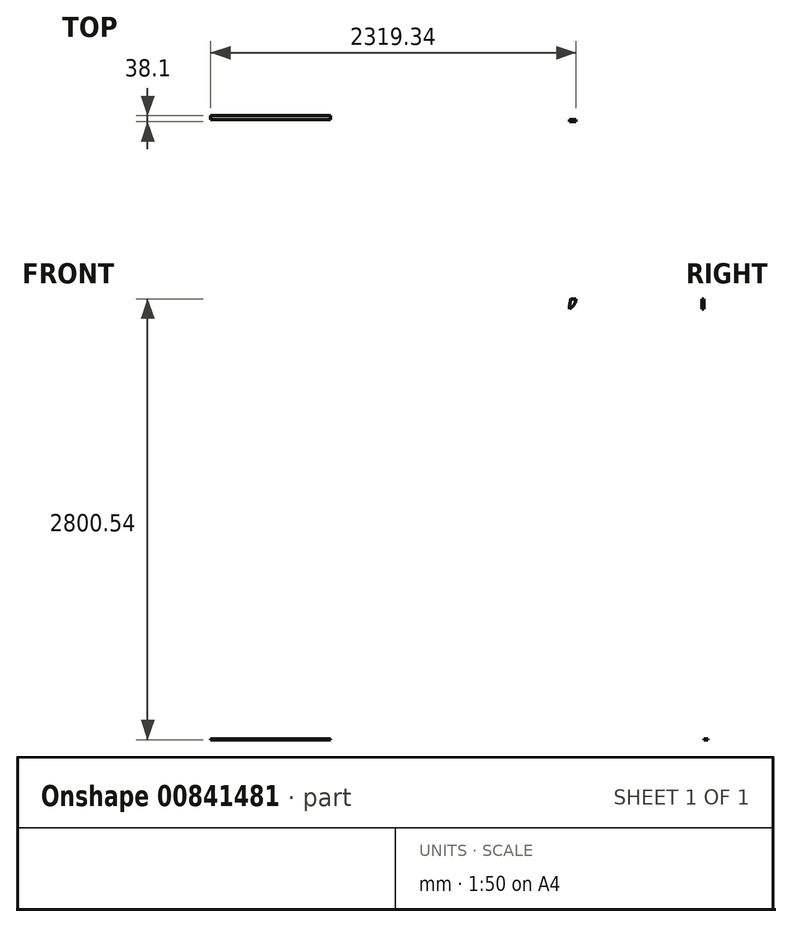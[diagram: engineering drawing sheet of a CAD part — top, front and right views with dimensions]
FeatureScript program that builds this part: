
annotation { "Feature Type Name" : "Feature", "Feature Type Description" : "" }
export const myFeature = defineFeature(function(context is Context, id is Id, definition is map)
    precondition{}
    {
        {
            var Q0;
            Q0=qCreatedBy(makeId("Front.planeOp"),FACE);
            var sketch = newSketch(context, id + "F0", { "sketchPlane" : qUnion([Q0])});
            skLineSegment(sketch, "E0.bottom", {"start": v(-2732.86, 2615) * mm, "end": v(264.34, 2615) * mm});
            skLineSegment(sketch, "E0.top", {"start": v(-2732.86, -179) * mm, "end": v(264.34, -179) * mm});
            skLineSegment(sketch, "E0.left", {"start": v(-2732.86, 2615) * mm, "end": v(-2732.86, -179) * mm});
            skLineSegment(sketch, "E0.right", {"start": v(264.34, 2615) * mm, "end": v(264.34, -179) * mm});
            skLineSegment(sketch, "E1", {"start": v(-2732.86, -179) * mm, "end": v(-2618.56, -179) * mm});
            skLineSegment(sketch, "E2", {"start": v(-2618.56, -179) * mm, "end": v(-1856.56, -179) * mm});
            skLineSegment(sketch, "E3.bottom", {"start": v(-2618.56, -175.37) * mm, "end": v(-1856.56, -175.37) * mm});
            skLineSegment(sketch, "E3.top", {"start": v(-2618.56, -185.53) * mm, "end": v(-1856.56, -185.53) * mm});
            skLineSegment(sketch, "E3.left", {"start": v(-2618.56, -175.37) * mm, "end": v(-2618.56, -185.53) * mm});
            skLineSegment(sketch, "E3.right", {"start": v(-1856.56, -175.37) * mm, "end": v(-1856.56, -185.53) * mm});
            skCircle(sketch, "E4", {"center": v(-2618.56, -179) * mm, "radius": 762 * mm});
            skLineSegment(sketch, "E5.bottom", {"start": v(-1795.4, -179) * mm, "end": v(-423.8, -179) * mm});
            skLineSegment(sketch, "E5.top", {"start": v(-1795.4, 1737.25) * mm, "end": v(-423.8, 1737.25) * mm});
            skLineSegment(sketch, "E5.left", {"start": v(-1795.4, -179) * mm, "end": v(-1795.4, 1737.25) * mm});
            skLineSegment(sketch, "E5.right", {"start": v(-423.8, -179) * mm, "end": v(-423.8, 1737.25) * mm});
            skLineSegment(sketch, "E6.bottom", {"start": v(-423.8, -179) * mm, "end": v(71.5, -179) * mm});
            skLineSegment(sketch, "E6.top", {"start": v(-423.8, 227.4) * mm, "end": v(71.5, 227.4) * mm});
            skLineSegment(sketch, "E6.left", {"start": v(-423.8, -179) * mm, "end": v(-423.8, 227.4) * mm});
            skLineSegment(sketch, "E6.right", {"start": v(71.5, -179) * mm, "end": v(71.5, 227.4) * mm});
            skLineSegment(sketch, "E7.bottom", {"start": v(71.5, 98.73) * mm, "end": v(264.34, 98.73) * mm});
            skLineSegment(sketch, "E7.top", {"start": v(71.5, -179) * mm, "end": v(264.34, -179) * mm});
            skLineSegment(sketch, "E7.left", {"start": v(71.5, 98.73) * mm, "end": v(71.5, -179) * mm});
            skLineSegment(sketch, "E7.right", {"start": v(264.34, 98.73) * mm, "end": v(264.34, -179) * mm});
            skLineSegment(sketch, "E8.bottom", {"start": v(-1541.48, 2615) * mm, "end": v(-855.68, 2615) * mm});
            skLineSegment(sketch, "E8.top", {"start": v(-1541.48, 2170.5) * mm, "end": v(-855.68, 2170.5) * mm});
            skLineSegment(sketch, "E8.left", {"start": v(-1541.48, 2615) * mm, "end": v(-1541.48, 2170.5) * mm});
            skLineSegment(sketch, "E8.right", {"start": v(-855.68, 2615) * mm, "end": v(-855.68, 2170.5) * mm});
            skCircle(sketch, "E9", {"center": v(-367.69, 2615) * mm, "radius": 68.47 * mm});
            skCircle(sketch, "E10", {"center": v(264.34, 721.56) * mm, "radius": 80.06 * mm});
            skCircle(sketch, "E11", {"center": v(-774.92, -179) * mm, "radius": 75.06 * mm});
            skLineSegment(sketch, "E12", {"start": v(264.34, 2615) * mm, "end": v(264.34, 2488) * mm});
            skCircle(sketch, "E13", {"center": v(264.34, 2488) * mm, "radius": 609.6 * mm});
            skSolve(sketch);
        }
        {
            var Q0;
            {var subQ0=sQuery(id+"F0.wireOp",EDGE,"E9");var subQ1=sQuery(id+"F0.wireOp",EDGE,"E0.bottom");var subQ2=makeQuery(id+"F0.imprint","INTERSECT",VERTEX,{"disambiguationData":[OD(1.0)],"derivedFrom":[subQ1,subQ0]});var subQ7=makeQuery(id+"F0.imprint","INTERSECT",VERTEX,{"disambiguationData":[OD(0.0)],"derivedFrom":[subQ1,subQ0]});Q0=qUnion([makeQuery(id+"F0.imprint","IMPRINT",FACE,{"disambiguationData":[TD([[makeQuery(id+"F0.imprint","IMPRINT",EDGE,{"disambiguationData":[TD([[subQ7,1.0]])],"derivedFrom":subQ1}),-1.0]])]}),makeQuery(id+"F0.imprint","IMPRINT",FACE,{"disambiguationData":[TD([[makeQuery(id+"F0.imprint","IMPRINT",EDGE,{"disambiguationData":[TD([[subQ2,-1.0]])],"derivedFrom":subQ1}),-1.0]])]})]);}
            var sketch = newSketch(context, id + "F1", { "sketchPlane" : qUnion([Q0])});
            skLineSegment(sketch, "E14.bottom", {"start": v(-5527.64, 1733.1) * mm, "end": v(-3609.94, 1733.1) * mm});
            skLineSegment(sketch, "E14.top", {"start": v(-5527.64, 412.3) * mm, "end": v(-3609.94, 412.3) * mm});
            skLineSegment(sketch, "E14.left", {"start": v(-5527.64, 1733.1) * mm, "end": v(-5527.64, 412.3) * mm});
            skLineSegment(sketch, "E14.right", {"start": v(-3609.94, 1733.1) * mm, "end": v(-3609.94, 412.3) * mm});
            skSolve(sketch);
        }
        {
            var Q0;
            {var subQ0=sQuery(id+"F0.wireOp",EDGE,"E3.left");var subQ3=sQuery(id+"F0.wireOp",EDGE,"E0.top");var subQ4=makeQuery(id+"F0.imprint","INTERSECT",VERTEX,{"derivedFrom":[subQ3,subQ0]});Q0=makeQuery(id+"F0.imprint","IMPRINT",FACE,{"disambiguationData":[TD([[makeQuery(id+"F0.imprint","IMPRINT",EDGE,{"disambiguationData":[TD([[subQ4,-1.0]])],"derivedFrom":subQ3}),-1.0]])]});}
            extrude(context, id + "F2", {"entities" : qUnion([Q0]), "oppositeDirection" : true, "depth" : 25.4 * mm, "offsetDistance" : 25.4 * mm});
        }
        {
            var Q0;
            {var subQ0=sQuery(id+"F0.wireOp",EDGE,"E9");var subQ1=sQuery(id+"F0.wireOp",EDGE,"E0.bottom");var subQ2=makeQuery(id+"F0.imprint","INTERSECT",VERTEX,{"disambiguationData":[OD(0.0)],"derivedFrom":[subQ1,subQ0]});var subQ7=makeQuery(id+"F0.imprint","INTERSECT",VERTEX,{"disambiguationData":[OD(1.0)],"derivedFrom":[subQ1,subQ0]});Q0=qUnion([makeQuery(id+"F1.imprint","IMPRINT",FACE,{"disambiguationData":[TD([[makeQuery(id+"F1.imprint","IMPRINT",EDGE,{"derivedFrom":makeQuery(id+"F0.imprint","IMPRINT",EDGE,{"disambiguationData":[TD([[subQ7,-1.0]])],"derivedFrom":subQ1})}),-1.0]])]}),makeQuery(id+"F1.imprint","IMPRINT",FACE,{"disambiguationData":[TD([[makeQuery(id+"F1.imprint","IMPRINT",EDGE,{"derivedFrom":makeQuery(id+"F0.imprint","IMPRINT",EDGE,{"disambiguationData":[TD([[subQ2,1.0]])],"derivedFrom":subQ1})}),-1.0]])]})]);}
            extrude(context, id + "F3", {"entities" : qUnion([Q0]), "depth" : 12.7 * mm, "offsetDistance" : 25.4 * mm});
        }
    });
